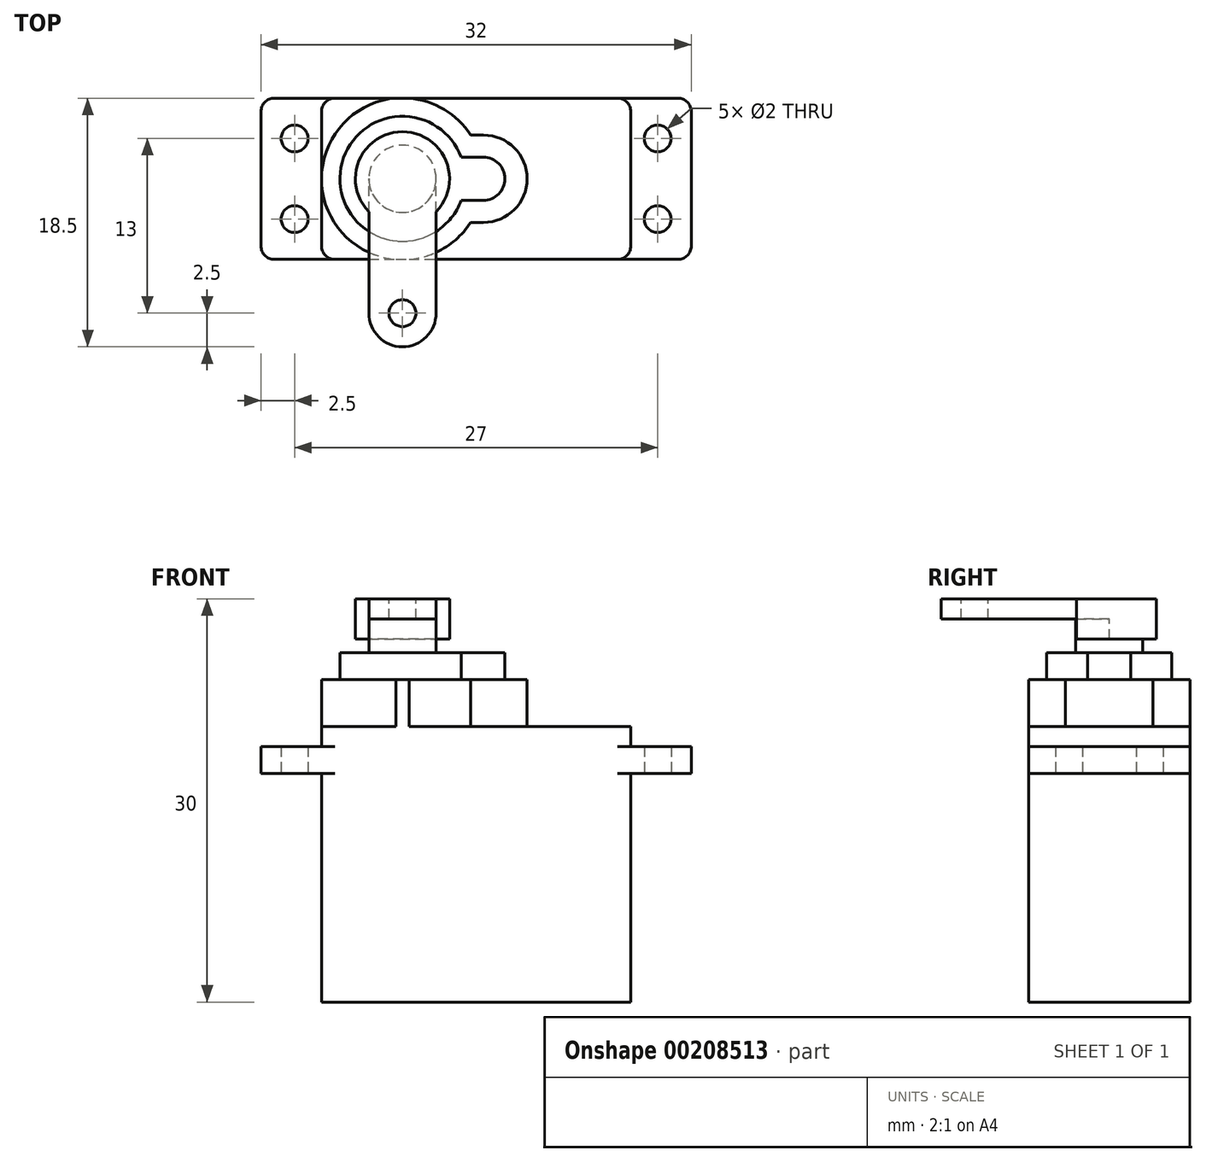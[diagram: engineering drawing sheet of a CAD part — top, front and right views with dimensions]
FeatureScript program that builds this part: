
annotation { "Feature Type Name" : "Feature", "Feature Type Description" : "" }
export const myFeature = defineFeature(function(context is Context, id is Id, definition is map)
    precondition{}
    {
        {
            var Q0;
            Q0=qCreatedBy(makeId("Top.planeOp"),FACE);
            var sketch = newSketch(context, id + "F0", { "sketchPlane" : qUnion([Q0])});
            skLineSegment(sketch, "E0.bottom", {"start": v(-6.02, 6) * mm, "end": v(16.98, 6) * mm});
            skLineSegment(sketch, "E0.top", {"start": v(-6.02, -6) * mm, "end": v(16.98, -6) * mm});
            skLineSegment(sketch, "E0.left", {"start": v(-6.02, 6) * mm, "end": v(-6.02, -6) * mm});
            skLineSegment(sketch, "E0.right", {"start": v(16.98, 6) * mm, "end": v(16.98, -6) * mm});
            skPoint(sketch, "E1", {"position": v(0, 0) * mm});
            skPoint(sketch, "E1.positionSnap0", {"position": v(-6.02, 0) * mm});
            skSolve(sketch);
        }
        {
            var Q0;
            Q0=makeQuery(id+"F0.imprint","IMPRINT",FACE,{"disambiguationData":[TD([[makeQuery(id+"F0.imprint","IMPRINT",EDGE,{"derivedFrom":sQuery(id+"F0.wireOp",EDGE,"E0.bottom")}),-1.0]])]});
            extrude(context, id + "F1", {"entities" : qUnion([Q0]), "oppositeDirection" : true, "depth" : 17 * mm});
        }
        {
            var Q0;
            Q0=makeQuery(id+"F0.imprint","IMPRINT",FACE,{"disambiguationData":[TD([[makeQuery(id+"F0.imprint","IMPRINT",EDGE,{"derivedFrom":sQuery(id+"F0.wireOp",EDGE,"E0.bottom")}),-1.0]])]});
            var sketch = newSketch(context, id + "F2", { "sketchPlane" : qUnion([Q0])});
            skLineSegment(sketch, "E2.bottom", {"start": v(-10.52, 6) * mm, "end": v(21.48, 6) * mm});
            skLineSegment(sketch, "E2.top", {"start": v(-10.52, -6) * mm, "end": v(21.48, -6) * mm});
            skLineSegment(sketch, "E2.left", {"start": v(-10.52, 6) * mm, "end": v(-10.52, -6) * mm});
            skLineSegment(sketch, "E2.right", {"start": v(21.48, 6) * mm, "end": v(21.48, -6) * mm});
            skPoint(sketch, "E3", {"position": v(5.48, 6) * mm});
            skLineSegment(sketch, "E4", {"start": v(5.48, 6) * mm, "end": v(5.48, -9.84) * mm, "construction": true});
            skCircle(sketch, "E5", {"center": v(-8.02, 3) * mm, "radius": 1 * mm});
            skCircle(sketch, "E6", {"center": v(-8.02, -3) * mm, "radius": 1 * mm});
            skLineSegment(sketch, "E7", {"start": v(-8.02, 3) * mm, "end": v(-8.02, -3) * mm, "construction": true});
            skLineSegment(sketch, "E8", {"start": v(0, 0) * mm, "end": v(-12.37, 0) * mm, "construction": true});
            skPoint(sketch, "E9", {"position": v(-8.02, 0) * mm});
            skCircle(sketch, "E10.MirrorC", {"center": v(18.98, 3) * mm, "radius": 1 * mm});
            skCircle(sketch, "E11.MirrorC", {"center": v(18.98, -3) * mm, "radius": 1 * mm});
            skSolve(sketch);
        }
        {
            var Q0;
            Q0 = qSketchRegion(id + "F2", true);
            extrude(context, id + "F3", {"entities" : qUnion([Q0]), "operationType" : NewBodyOperationType.ADD, "depth" : 2 * mm});
        }
        {
            var Q0;
            Q0=makeQuery(id+"F1.opExtrude","CAP_FACE",FACE,{"disambiguationData":[OSD([sQuery(id+"F0.wireOp",EDGE,"E0.bottom"),sQuery(id+"F0.wireOp",EDGE,"E0.top"),sQuery(id+"F0.wireOp",EDGE,"E0.left"),sQuery(id+"F0.wireOp",EDGE,"E0.right")])],"isStart":false});
            var sketch = newSketch(context, id + "F4", { "sketchPlane" : qUnion([Q0])});
            skArc(sketch, "E12", {"start": v(5.07, 3.25) * mm, "mid": v(-5.95, -0.9) * mm, "end": v(5.8, -1.6) * mm});
            skArc(sketch, "E13", {"start": v(6.02, -3.25) * mm, "mid": v(9.27, 0) * mm, "end": v(6.02, 3.25) * mm});
            skLineSegment(sketch, "E14", {"start": v(6.02, 3.25) * mm, "end": v(5.07, 3.25) * mm});
            skLineSegment(sketch, "E15", {"start": v(0, 0) * mm, "end": v(6.02, 0) * mm, "construction": true});
            skLineSegment(sketch, "E16.MirrorCS", {"start": v(6.02, -3.25) * mm, "end": v(5.07, -3.25) * mm});
            skLineSegment(sketch, "E17", {"start": v(6.02, 1.6) * mm, "end": v(4.37, 1.6) * mm});
            skLineSegment(sketch, "E18.MirrorCS", {"start": v(6.02, -1.6) * mm, "end": v(4.37, -1.6) * mm});
            skArc(sketch, "E19.trimOffspring", {"start": v(6.02, -1.6) * mm, "mid": v(7.62, 0) * mm, "end": v(6.02, 1.6) * mm});
            skCircle(sketch, "E20", {"center": v(0, 0) * mm, "radius": 4.65 * mm});
            skSolve(sketch);
        }
        {
            var Q0;
            Q0=makeQuery(id+"F4.imprint","IMPRINT",FACE,{"disambiguationData":[TD([[makeQuery(id+"F4.imprint","IMPRINT",EDGE,{"derivedFrom":sQuery(id+"F4.wireOp",EDGE,"E13")}),1.0]])]});
            var Q1;
            {var subQ0=sQuery(id+"F4.wireOp",EDGE,"E20");var subQ1=makeQuery(id+"F4.imprint","INTERSECT",VERTEX,{"derivedFrom":[sQuery(id+"F4.wireOp",EDGE,"E17"),subQ0]});Q1=makeQuery(id+"F4.imprint","IMPRINT",FACE,{"disambiguationData":[TD([[makeQuery(id+"F4.imprint","IMPRINT",EDGE,{"disambiguationData":[TD([[subQ1,-1.0]])],"derivedFrom":subQ0}),1.0]])]});}
            var Q2;
            {var subQ1=sQuery(id+"F4.wireOp",EDGE,"E17");Q2=makeQuery(id+"F4.imprint","IMPRINT",FACE,{"disambiguationData":[TD([[makeQuery(id+"F4.imprint","IMPRINT",EDGE,{"derivedFrom":subQ1}),1.0]])]});}
            extrude(context, id + "F5", {"entities" : qUnion([Q0, Q1, Q2]), "operationType" : NewBodyOperationType.ADD, "oppositeDirection" : true, "depth" : 24 * mm});
        }
        {
            var Q0;
            {var subQ0=sQuery(id+"F4.wireOp",EDGE,"E20");var subQ1=makeQuery(id+"F4.imprint","INTERSECT",VERTEX,{"derivedFrom":[sQuery(id+"F4.wireOp",EDGE,"E17"),subQ0]});Q0=makeQuery(id+"F4.imprint","IMPRINT",FACE,{"disambiguationData":[TD([[makeQuery(id+"F4.imprint","IMPRINT",EDGE,{"disambiguationData":[TD([[subQ1,-1.0]])],"derivedFrom":subQ0}),1.0]])]});}
            var Q1;
            {var subQ1=sQuery(id+"F4.wireOp",EDGE,"E17");Q1=makeQuery(id+"F4.imprint","IMPRINT",FACE,{"disambiguationData":[TD([[makeQuery(id+"F4.imprint","IMPRINT",EDGE,{"derivedFrom":subQ1}),1.0]])]});}
            extrude(context, id + "F6", {"entities" : qUnion([Q0, Q1]), "operationType" : NewBodyOperationType.ADD, "oppositeDirection" : true, "depth" : 26 * mm});
        }
        {
            var Q0;
            Q0 = qSketchRegion(id + "F0", true);
            extrude(context, id + "F7", {"entities" : qUnion([Q0]), "operationType" : NewBodyOperationType.ADD, "depth" : 3.5 * mm});
        }
        {
            var Q0;
            Q0=makeQuery(id+"F1.opExtrude","SWEPT_EDGE",EDGE,{"disambiguationData":[OSD([sQuery(id+"F0.wireOp",EDGE,"E0.top"),sQuery(id+"F0.wireOp",EDGE,"E0.right")])]});
            var Q1;
            Q1=makeQuery(id+"F1.opExtrude","SWEPT_EDGE",EDGE,{"disambiguationData":[OSD([sQuery(id+"F0.wireOp",EDGE,"E0.bottom"),sQuery(id+"F0.wireOp",EDGE,"E0.right")])]});
            var Q2;
            Q2=makeQuery(id+"F1.opExtrude","SWEPT_EDGE",EDGE,{"disambiguationData":[OSD([sQuery(id+"F0.wireOp",EDGE,"E0.top"),sQuery(id+"F0.wireOp",EDGE,"E0.left")])]});
            var Q3;
            Q3=makeQuery(id+"F1.opExtrude","SWEPT_EDGE",EDGE,{"disambiguationData":[OSD([sQuery(id+"F0.wireOp",EDGE,"E0.bottom"),sQuery(id+"F0.wireOp",EDGE,"E0.left")])]});
            var Q4;
            Q4=makeQuery(id+"F3.opExtrude","SWEPT_EDGE",EDGE,{"disambiguationData":[OSD([sQuery(id+"F2.wireOp",EDGE,"E2.top"),sQuery(id+"F2.wireOp",EDGE,"E2.left")])]});
            var Q5;
            Q5=makeQuery(id+"F3.opExtrude","SWEPT_EDGE",EDGE,{"disambiguationData":[OSD([sQuery(id+"F2.wireOp",EDGE,"E2.bottom"),sQuery(id+"F2.wireOp",EDGE,"E2.left")])]});
            var Q6;
            Q6=makeQuery(id+"F3.opExtrude","SWEPT_EDGE",EDGE,{"disambiguationData":[OSD([sQuery(id+"F2.wireOp",EDGE,"E2.bottom"),sQuery(id+"F2.wireOp",EDGE,"E2.right")])]});
            var Q7;
            Q7=makeQuery(id+"F3.opExtrude","SWEPT_EDGE",EDGE,{"disambiguationData":[OSD([sQuery(id+"F2.wireOp",EDGE,"E2.top"),sQuery(id+"F2.wireOp",EDGE,"E2.right")])]});
            var Q8;
            Q8=makeQuery(id+"F7.opExtrude","SWEPT_EDGE",EDGE,{"disambiguationData":[OSD([sQuery(id+"F0.wireOp",EDGE,"E0.bottom"),sQuery(id+"F0.wireOp",EDGE,"E0.right")])]});
            var Q9;
            Q9=makeQuery(id+"F7.opExtrude","SWEPT_EDGE",EDGE,{"disambiguationData":[OSD([sQuery(id+"F0.wireOp",EDGE,"E0.top"),sQuery(id+"F0.wireOp",EDGE,"E0.right")])]});
            var Q10;
            Q10=makeQuery(id+"F7.opExtrude","SWEPT_EDGE",EDGE,{"disambiguationData":[OSD([sQuery(id+"F0.wireOp",EDGE,"E0.bottom"),sQuery(id+"F0.wireOp",EDGE,"E0.left")])]});
            var Q11;
            Q11=makeQuery(id+"F7.opExtrude","SWEPT_EDGE",EDGE,{"disambiguationData":[OSD([sQuery(id+"F0.wireOp",EDGE,"E0.top"),sQuery(id+"F0.wireOp",EDGE,"E0.left")])]});
            fillet(context, id + "F8", {"entities" : qUnion([Q0, Q1, Q2, Q3, Q4, Q5, Q6, Q7, Q8, Q9, Q10, Q11]), "radius" : 1 * mm, "tangentPropagation" : true, "allowEdgeOverflow" : false});
        }
        {
            var Q0;
            {var subQ0=sQuery(id+"F4.wireOp",EDGE,"E20");var subQ1=makeQuery(id+"F4.imprint","INTERSECT",VERTEX,{"derivedFrom":[sQuery(id+"F4.wireOp",EDGE,"E17"),subQ0]});Q0=makeQuery(id+"F4.imprint","IMPRINT",FACE,{"disambiguationData":[TD([[makeQuery(id+"F4.imprint","IMPRINT",EDGE,{"disambiguationData":[TD([[subQ1,-1.0]])],"derivedFrom":subQ0}),1.0]])]});}
            var sketch = newSketch(context, id + "F9", { "sketchPlane" : qUnion([Q0])});
            skCircle(sketch, "E21", {"center": v(0, 0) * mm, "radius": 2.5 * mm});
            skSolve(sketch);
        }
        {
            var Q0;
            Q0 = qSketchRegion(id + "F9", true);
            extrude(context, id + "F10", {"entities" : qUnion([Q0]), "operationType" : NewBodyOperationType.ADD, "oppositeDirection" : true, "depth" : (13 + 17) * mm});
        }
        {
            var Q0;
            Q0=makeQuery(id+"F10.opExtrude","CAP_FACE",FACE,{"disambiguationData":[OSD([sQuery(id+"F9.wireOp",EDGE,"E21")])],"isStart":false});
            var sketch = newSketch(context, id + "F11", { "sketchPlane" : qUnion([Q0])});
            skLineSegment(sketch, "E22", {"start": v(0, 0) * mm, "end": v(0, -6.92) * mm, "construction": true});
            skLineSegment(sketch, "E23", {"start": v(2.5, -10) * mm, "end": v(2.5, 0) * mm});
            skCircle(sketch, "E24", {"center": v(0, -10) * mm, "radius": 2.5 * mm});
            skLineSegment(sketch, "E25.MirrorCS", {"start": v(-2.5, -10) * mm, "end": v(-2.5, 0) * mm});
            skCircle(sketch, "E26", {"center": v(0, -10) * mm, "radius": 1 * mm});
            skLineSegment(sketch, "E27", {"start": v(2.5, 0) * mm, "end": v(-2.5, 0) * mm});
            skCircle(sketch, "E28", {"center": v(0, 0) * mm, "radius": 3.5 * mm});
            skSolve(sketch);
        }
        {
            var Q0;
            {var subQ0=sQuery(id+"F11.wireOp",EDGE,"E24");var subQ1=sQuery(id+"F11.wireOp",EDGE,"E23");var subQ2=makeQuery(id+"F11.imprint","INTERSECT",VERTEX,{"derivedFrom":[subQ1,subQ0]});Q0=makeQuery(id+"F11.imprint","IMPRINT",FACE,{"disambiguationData":[TD([[makeQuery(id+"F11.imprint","IMPRINT",EDGE,{"disambiguationData":[TD([[subQ2,-1.0]])],"derivedFrom":subQ1}),1.0]])]});}
            var Q1;
            {var subQ1=sQuery(id+"F11.wireOp",EDGE,"E23");var subQ4=sQuery(id+"F11.wireOp",EDGE,"E28");var subQ5=makeQuery(id+"F11.imprint","INTERSECT",VERTEX,{"derivedFrom":[subQ1,subQ4]});Q1=makeQuery(id+"F11.imprint","IMPRINT",FACE,{"disambiguationData":[TD([[makeQuery(id+"F11.imprint","IMPRINT",EDGE,{"disambiguationData":[TD([[subQ5,1.0]])],"derivedFrom":subQ4}),1.0]])]});}
            var Q2;
            Q2=makeQuery(id+"F11.imprint","IMPRINT",FACE,{"disambiguationData":[TD([[makeQuery(id+"F11.imprint","IMPRINT",EDGE,{"derivedFrom":sQuery(id+"F11.wireOp",EDGE,"E26")}),-1.0]])]});
            extrude(context, id + "F12", {"entities" : qUnion([Q0, Q1, Q2]), "oppositeDirection" : true, "depth" : 1.5 * mm});
        }
        {
            var Q0;
            {var subQ1=sQuery(id+"F11.wireOp",EDGE,"E23");var subQ4=sQuery(id+"F11.wireOp",EDGE,"E28");var subQ5=makeQuery(id+"F11.imprint","INTERSECT",VERTEX,{"derivedFrom":[subQ1,subQ4]});Q0=makeQuery(id+"F11.imprint","IMPRINT",FACE,{"disambiguationData":[TD([[makeQuery(id+"F11.imprint","IMPRINT",EDGE,{"disambiguationData":[TD([[subQ5,-1.0]])],"derivedFrom":subQ4}),1.0]])]});}
            extrude(context, id + "F13", {"entities" : qUnion([Q0]), "operationType" : NewBodyOperationType.ADD, "oppositeDirection" : true, "depth" : 3 * mm});
        }
    });
